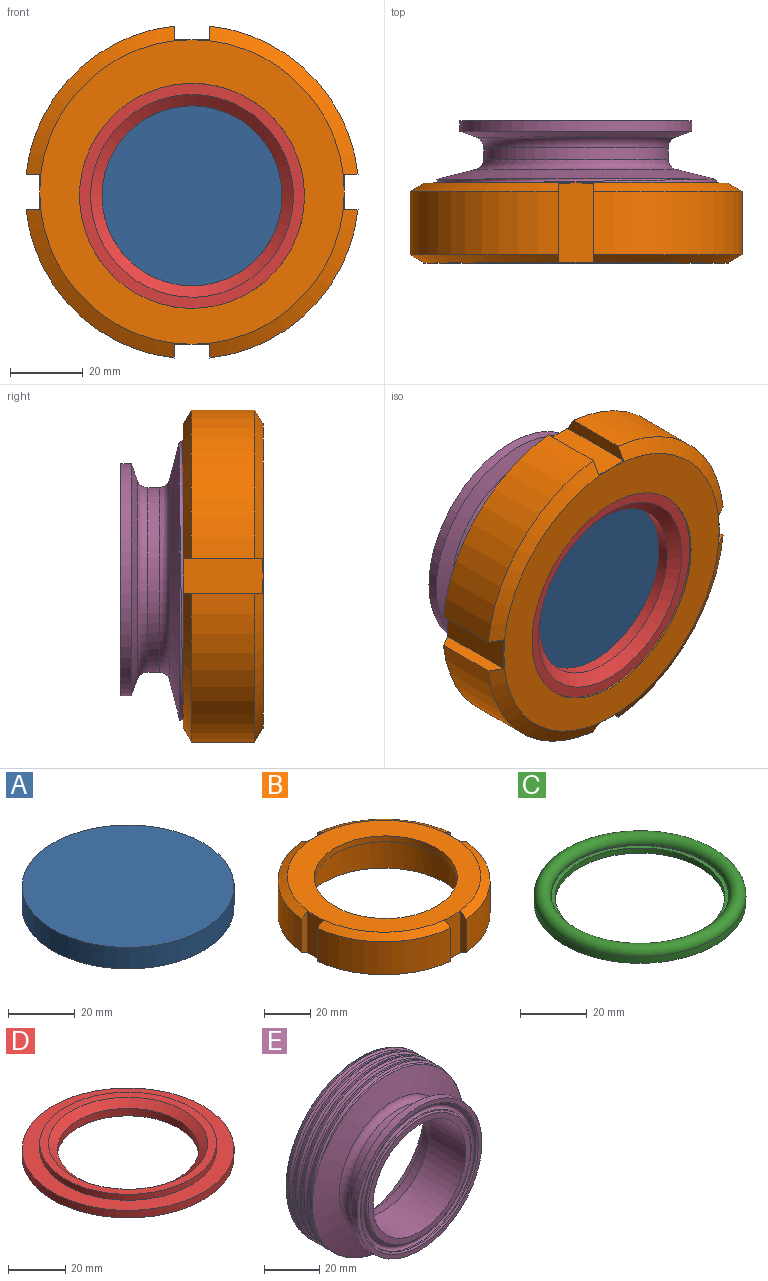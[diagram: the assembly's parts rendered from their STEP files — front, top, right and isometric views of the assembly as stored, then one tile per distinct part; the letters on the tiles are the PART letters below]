
ASSEMBLY  parts=5 mates=4
PART A: 3 faces, bbox 63.5x63.5x7.8 mm
  f0: cylinder r=31.75mm len=63.5mm, axis (0,0,-1), area 1565.7mm2, adj f1,f2
  f1: plane 63.5x63.5mm, normal (0,0,1), area 3166.9mm2, adj f0
  f2: plane 63.5x63.5mm, normal (0,0,-1), area 3166.9mm2, adj f0
PART B: 29 faces, bbox 92x92x22 mm
  f0: cylinder r=45.97mm len=40.88mm, axis (0,0,-1), area 1091mm2, adj f4,f8,f16,f25
  f1: cylinder r=45.97mm len=40.88mm, axis (0,0,-1), area 1091mm2, adj f5,f9,f20,f24
  f2: cylinder r=45.97mm len=40.88mm, axis (0,0,-1), area 1091mm2, adj f6,f10,f17,f22
  f3: cylinder r=45.97mm len=40.88mm, axis (0,0,-1), area 1091mm2, adj f7,f11,f14,f19
  f4: cone r=45.97mm half-angle=60.5deg, axis (0,0,1), area 276.4mm2, adj f0,f13,f15,f16,f23,f25
  f5: cone r=45.97mm half-angle=60.5deg, axis (0,0,1), area 276.4mm2, adj f1,f13,f20,f21,f23,f24
  f6: cone r=45.97mm half-angle=60.5deg, axis (0,0,1), area 276.4mm2, adj f2,f13,f17,f18,f21,f22
  f7: cone r=45.97mm half-angle=60.5deg, axis (0,0,1), area 276.4mm2, adj f3,f13,f14,f15,f18,f19
  f8: cone r=41.94mm half-angle=60.5deg, axis (0,0,-1), area 276.4mm2, adj f0,f12,f15,f16,f23,f25
  f9: cone r=41.94mm half-angle=60.5deg, axis (0,0,-1), area 276.4mm2, adj f1,f12,f20,f21,f23,f24
  f10: cone r=41.94mm half-angle=60.5deg, axis (0,0,-1), area 276.4mm2, adj f2,f12,f17,f18,f21,f22
  f11: cone r=41.94mm half-angle=60.5deg, axis (0,0,-1), area 276.4mm2, adj f3,f12,f14,f15,f18,f19
  f12: plane 83.87x83.87mm, normal (0,0,1), area 2508mm2, adj f8,f9,f10,f11,f28
  f13: plane 83.87x83.87mm, normal (0,0,-1), area 1159.8mm2, adj f4,f5,f6,f7,f27
  f14: plane 21.72x3.8mm, normal (0,-1,0), area 74.1mm2, adj f3,f7,f11,f15
  f15: plane 22.03x9.69mm, normal (1,0,0), area 212.1mm2, adj f4,f7,f8,f11,f14,f16
  f16: plane 21.72x3.8mm, normal (0,1,0), area 74.1mm2, adj f0,f4,f8,f15
  f17: plane 21.72x3.8mm, normal (1,0,0), area 74.1mm2, adj f2,f6,f10,f18
  f18: plane 22.03x9.69mm, normal (0,1,0), area 212.1mm2, adj f6,f7,f10,f11,f17,f19
  f19: plane 21.72x3.8mm, normal (-1,0,0), area 74.1mm2, adj f3,f7,f11,f18
  f20: plane 21.72x3.8mm, normal (0,1,0), area 74.1mm2, adj f1,f5,f9,f21
  f21: plane 22.03x9.69mm, normal (-1,0,0), area 212.1mm2, adj f5,f6,f9,f10,f20,f22
  f22: plane 21.72x3.8mm, normal (0,-1,0), area 74.1mm2, adj f2,f6,f10,f21
  f23: plane 22.03x9.69mm, normal (0,-1,0), area 212.1mm2, adj f4,f5,f8,f9,f24,f25
  f24: plane 21.72x3.8mm, normal (1,0,0), area 74.1mm2, adj f1,f5,f9,f23
  f25: plane 21.72x3.8mm, normal (-1,0,0), area 74.1mm2, adj f0,f4,f8,f23
  f26: plane 74.55x74.55mm, normal (0,0,-1), area 1348.2mm2, adj f27,f28
  f27: cylinder r=37.27mm len=74.55mm, axis (0,0,-1), area 4431.8mm2, adj f13,f26
  f28: cylinder r=30.99mm len=61.98mm, axis (0,0,1), area 603.3mm2, adj f12,f26
PART C: 6 faces, bbox 68.7x68.7x5 mm
  f0: plane 53.34x53.34mm, normal (0,0,1), area 207.8mm2, adj f1,f4
  f1: cylinder r=25.4mm len=50.8mm, axis (0,0,-1), area 304mm2, adj f0,f3
  f2: cylinder r=31.75mm len=63.5mm, axis (0,0,-1), area 481.4mm2, adj f3,f5
  f3: plane 63.5x63.5mm, normal (0,0,-1), area 1140.1mm2, adj f1,f2
  f4: cylinder r=26.67mm len=53.34mm, axis (0,0,-1), area 85.1mm2, adj f0,f5
  f5: torus R=29.21mm, axis (0,0,-1), area 1464.5mm2, adj f2,f4
PART D: 7 faces, bbox 74.4x74.4x5.8 mm
  f0: cylinder r=24.8mm len=49.61mm, axis (0,0,-1), area 502.7mm2, adj f3,f4
  f1: cylinder r=37.19mm len=74.37mm, axis (0,0,-1), area 753.7mm2, adj f2,f3
  f2: plane 74.37x74.37mm, normal (0,0,1), area 1319.9mm2, adj f1,f5
  f3: plane 74.37x74.37mm, normal (0,0,-1), area 2411.4mm2, adj f0,f1
  f4: cone r=24.8mm half-angle=50.6deg, axis (0,0,1), area 669.7mm2, adj f0,f6
  f5: cylinder r=31.03mm len=62.05mm, axis (0,0,-1), area 500.1mm2, adj f2,f6
  f6: plane 62.05x62.05mm, normal (0,0,1), area 573.9mm2, adj f4,f5
PART E: 29 faces, bbox 77.6x31.6x77.5 mm
  f0: plane 63.91x63.91mm, normal (0,-1,0), area 350.1mm2, adj f1,f11
  f1: torus R=30.16mm, axis (0,-1,0), area 172.1mm2, adj f0,f2
  f2: cone r=29.43mm half-angle=23deg, axis (0,-1,0), area 78.8mm2, adj f1,f3
  f3: torus R=28.17mm, axis (0,-1,0), area 494.2mm2, adj f2,f4
  f4: cone r=27.07mm half-angle=23deg, axis (0,1,0), area 72.4mm2, adj f3,f5
  f5: torus R=26.18mm, axis (0,-1,0), area 153.8mm2, adj f4,f6
  f6: plane 52.36x52.36mm, normal (0,-1,0), area 381mm2, adj f5,f7
  f7: cylinder r=23.75mm len=47.5mm, axis (0,-1,0), area 2772.5mm2, adj f6,f19
  f8: cylinder r=25.4mm len=50.8mm, axis (0,-1,0), area 494.7mm2, adj f9,f21
  f9: torus R=28.57mm, axis (0,-1,0), area 636.9mm2, adj f8,f10
  f10: cone r=27.49mm half-angle=70deg, axis (0,-1,0), area 887.1mm2, adj f9,f11
  f11: cylinder r=31.95mm len=63.91mm, axis (0,-1,0), area 571.1mm2, adj f0,f10
  f12: cone r=25.4mm half-angle=75.8deg, axis (0,1,0), area 2318.2mm2, adj f13,f21,f22,f23,f24
  f13: cylinder r=38.71mm len=77.42mm, axis (0,-1,0), area 561.5mm2, adj f12,f23,f24,f26
  f14: plane 76.09x76.08mm, normal (0,1,0), area 1055.7mm2, adj f20,f25,f26,f27,f28
  f15: cylinder r=31.93mm len=63.86mm, axis (0,-1,0), area 840.7mm2, adj f16,f20
  f16: plane 63.86x63.86mm, normal (0,1,0), area 916.5mm2, adj f15,f17
  f17: cylinder r=26.97mm len=53.95mm, axis (0,-1,0), area 538.1mm2, adj f16,f18
  f18: plane 53.95x53.95mm, normal (0,1,0), area 319.5mm2, adj f17,f19
  f19: cone r=25.02mm half-angle=15.8deg, axis (0,1,0), area 715.8mm2, adj f7,f18
  f20: cone r=33.2mm half-angle=11.3deg, axis (0,1,0), area 1324.9mm2, adj f14,f15
  f21: torus R=28.32mm, axis (0,-1,0), area 635.8mm2, adj f8,f12
  f22: bspline ~76.19x76.15mm, area 1191.4mm2, adj f12,f23,f24,f27
  f23: bspline ~77.45x77.44mm, area 989.4mm2, adj f12,f13,f22,f28
  f24: bspline ~77.45x77.44mm, area 1014.5mm2, adj f12,f13,f22,f25
  f25: bspline ~37.82x11.21mm, area 19.6mm2, adj f14,f24,f26,f27
  f26: cone r=38.71mm half-angle=45deg, axis (0,-1,0), area 25.5mm2, adj f13,f14,f25,f28
  f27: bspline ~65.92x63.6mm, area 72.3mm2, adj f14,f22,f25,f28
  f28: bspline ~36.94x13.54mm, area 29.9mm2, adj f14,f23,f26,f27
PLACE A rot(axis=(-1,0,0),90deg) t=(0,-32.83,0)mm
PLACE B rot(axis=(1,0,0),90deg) t=(0,-17.13,1.06)mm
PLACE C rot(axis=(-1,0,0),90deg) t=(0,-24.98,0)mm
PLACE D rot(axis=(1,0,0),90deg) t=(0,-32.83,0)mm
PLACE E rot(axis=(0,0,1),180deg) t=(0,0,0)mm
MATE fastened E.f1 <-> C.f4  axis (0,-1,0) through (0,-23.08,0)mm
MATE fastened D.f1 <-> A.f0  axis (0,1,0) through (0,-32.83,0)mm
MATE fastened C.f1 <-> A.f0  axis (0,-1,0) through (0,-24.98,0)mm
MATE fastened B.f28 <-> D.f4  axis (0,1,0) through (0,-36.06,0)mm
